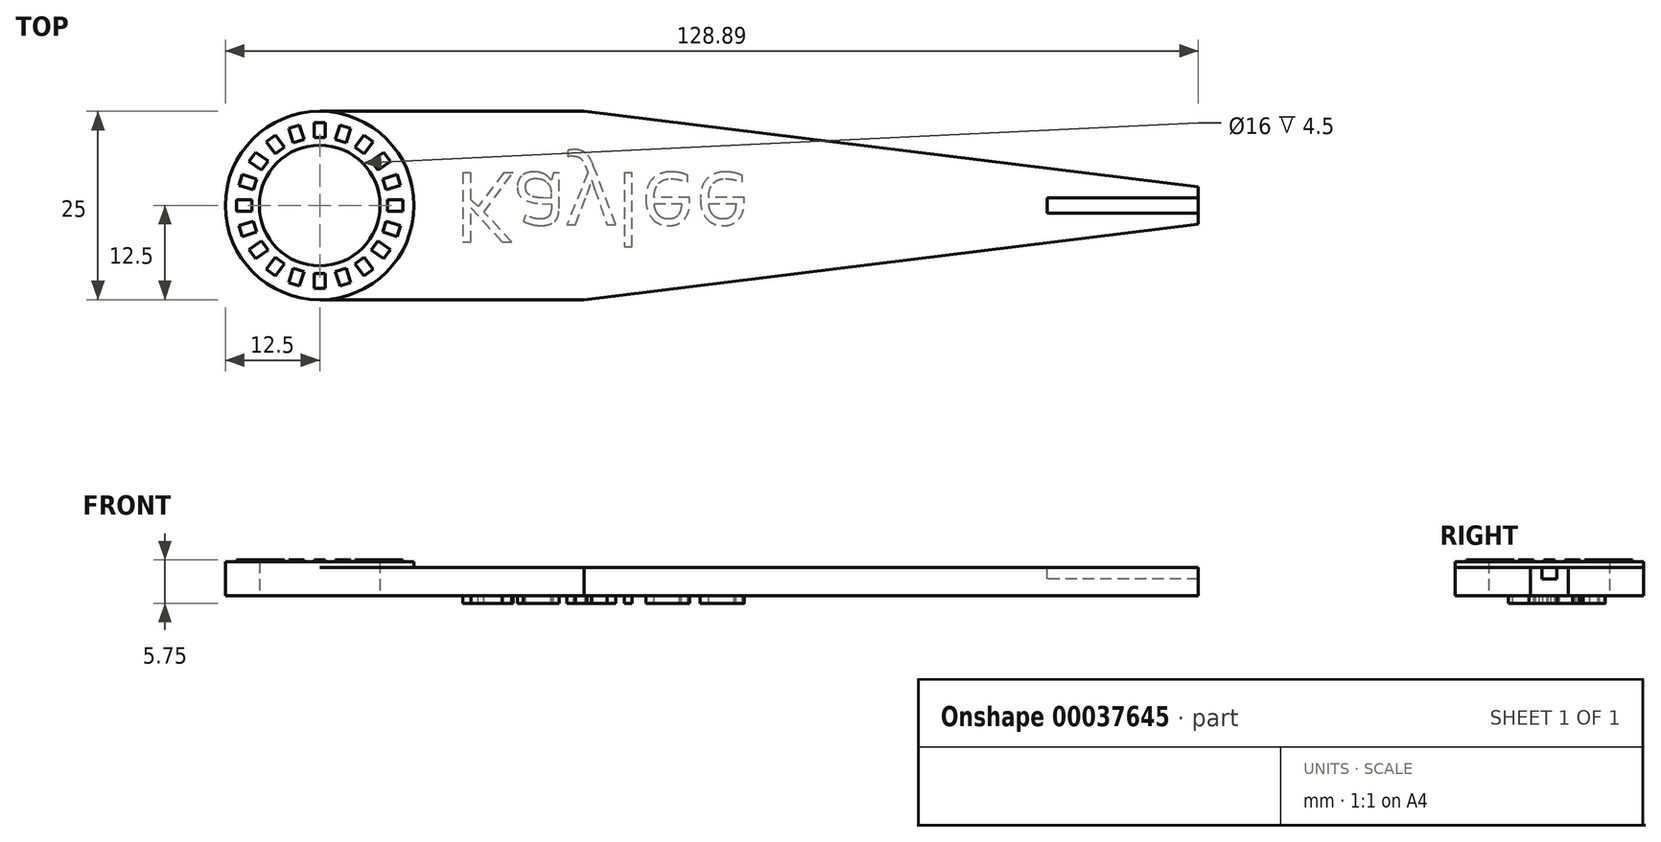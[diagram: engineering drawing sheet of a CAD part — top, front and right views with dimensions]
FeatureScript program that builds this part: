
annotation { "Feature Type Name" : "Feature", "Feature Type Description" : "" }
export const myFeature = defineFeature(function(context is Context, id is Id, definition is map)
    precondition{}
    {
        {
            var Q0;
            Q0=qCreatedBy(makeId("Top.planeOp"),FACE);
            var sketch = newSketch(context, id + "F0", { "sketchPlane" : qUnion([Q0])});
            skCircle(sketch, "E0", {"center": v(0, 0) * mm, "radius": 8 * mm});
            skCircle(sketch, "E1", {"center": v(0, 0) * mm, "radius": 12.5 * mm});
            skLineSegment(sketch, "E2", {"start": v(0, 12.5) * mm, "end": v(35, 12.5) * mm});
            skPoint(sketch, "E3", {"position": v(0, 12.5) * mm});
            skLineSegment(sketch, "E4", {"start": v(0, 0) * mm, "end": v(35.57, 0) * mm, "construction": true});
            skLineSegment(sketch, "E5.MirrorCS", {"start": v(0, -12.5) * mm, "end": v(35, -12.5) * mm});
            skLineSegment(sketch, "E6", {"start": v(35, 12.5) * mm, "end": v(74.56, 12.5) * mm, "construction": true});
            skLineSegment(sketch, "E7", {"start": v(35, 12.5) * mm, "end": v(116.39, 2.5) * mm});
            skLineSegment(sketch, "E8.MirrorCS", {"start": v(35, -12.5) * mm, "end": v(116.39, -2.5) * mm});
            skLineSegment(sketch, "E9", {"start": v(116.39, 2.5) * mm, "end": v(116.39, -2.5) * mm});
            skSolve(sketch);
        }
        {
            var Q0;
            Q0 = qSketchRegion(id + "F0", true);
            extrude(context, id + "F1", {"entities" : qUnion([Q0]), "depth" : 3.5 * mm});
        }
        {
            var Q0;
            Q0=makeQuery(id+"F1.opExtrude","CAP_FACE",FACE,{"disambiguationData":[OSD([sQuery(id+"F0.wireOp",EDGE,"E0"),sQuery(id+"F0.wireOp",EDGE,"E1"),sQuery(id+"F0.wireOp",EDGE,"E2"),sQuery(id+"F0.wireOp",EDGE,"E5.MirrorCS"),sQuery(id+"F0.wireOp",EDGE,"E7"),sQuery(id+"F0.wireOp",EDGE,"E8.MirrorCS"),sQuery(id+"F0.wireOp",EDGE,"E9")])],"isStart":false});
            var sketch = newSketch(context, id + "F2", { "sketchPlane" : qUnion([Q0])});
            skCircle(sketch, "E10", {"center": v(0, 0) * mm, "radius": 12.5 * mm});
            skCircle(sketch, "E11", {"center": v(0, 0) * mm, "radius": 8 * mm});
            skSolve(sketch);
        }
        {
            var Q0;
            Q0 = qSketchRegion(id + "F2", true);
            extrude(context, id + "F3", {"entities" : qUnion([Q0]), "operationType" : NewBodyOperationType.ADD, "depth" : 1 * mm});
        }
        {
            var Q0;
            Q0=makeQuery(id+"F3.opExtrude","CAP_FACE",FACE,{"disambiguationData":[OSD([sQuery(id+"F2.wireOp",EDGE,"E10"),sQuery(id+"F2.wireOp",EDGE,"E11")])],"isStart":false});
            var sketch = newSketch(context, id + "F4", { "sketchPlane" : qUnion([Q0])});
            skLineSegment(sketch, "E12.bottom", {"start": v(-0.75, 11) * mm, "end": v(0.75, 11) * mm});
            skLineSegment(sketch, "E12.top", {"start": v(-0.75, 9) * mm, "end": v(0.75, 9) * mm});
            skLineSegment(sketch, "E12.left", {"start": v(-0.75, 11) * mm, "end": v(-0.75, 9) * mm});
            skLineSegment(sketch, "E12.right", {"start": v(0.75, 11) * mm, "end": v(0.75, 9) * mm});
            skPoint(sketch, "E13", {"position": v(0, 8) * mm});
            skLineSegment(sketch, "E14.1.0", {"start": v(-4.11, 10.23) * mm, "end": v(-2.69, 10.7) * mm});
            skLineSegment(sketch, "E14.1.1", {"start": v(-4.11, 10.23) * mm, "end": v(-3.5, 8.33) * mm});
            skLineSegment(sketch, "E14.1.2", {"start": v(-3.5, 8.33) * mm, "end": v(-2.07, 8.8) * mm});
            skLineSegment(sketch, "E14.1.3", {"start": v(-2.69, 10.7) * mm, "end": v(-2.07, 8.8) * mm});
            skLineSegment(sketch, "E14.2.0", {"start": v(-7.07, 8.46) * mm, "end": v(-5.86, 9.34) * mm});
            skLineSegment(sketch, "E14.2.1", {"start": v(-7.07, 8.46) * mm, "end": v(-5.9, 6.84) * mm});
            skLineSegment(sketch, "E14.2.2", {"start": v(-5.9, 6.84) * mm, "end": v(-4.68, 7.72) * mm});
            skLineSegment(sketch, "E14.2.3", {"start": v(-5.86, 9.34) * mm, "end": v(-4.68, 7.72) * mm});
            skLineSegment(sketch, "E14.3.0", {"start": v(-9.34, 5.86) * mm, "end": v(-8.46, 7.07) * mm});
            skLineSegment(sketch, "E14.3.1", {"start": v(-9.34, 5.86) * mm, "end": v(-7.72, 4.68) * mm});
            skLineSegment(sketch, "E14.3.2", {"start": v(-7.72, 4.68) * mm, "end": v(-6.84, 5.9) * mm});
            skLineSegment(sketch, "E14.3.3", {"start": v(-8.46, 7.07) * mm, "end": v(-6.84, 5.9) * mm});
            skLineSegment(sketch, "E14.4.0", {"start": v(-10.7, 2.69) * mm, "end": v(-10.23, 4.11) * mm});
            skLineSegment(sketch, "E14.4.1", {"start": v(-10.7, 2.69) * mm, "end": v(-8.8, 2.07) * mm});
            skLineSegment(sketch, "E14.4.2", {"start": v(-8.8, 2.07) * mm, "end": v(-8.33, 3.5) * mm});
            skLineSegment(sketch, "E14.4.3", {"start": v(-10.23, 4.11) * mm, "end": v(-8.33, 3.5) * mm});
            skLineSegment(sketch, "E14.5.0", {"start": v(-11, -0.75) * mm, "end": v(-11, 0.75) * mm});
            skLineSegment(sketch, "E14.5.1", {"start": v(-11, -0.75) * mm, "end": v(-9, -0.75) * mm});
            skLineSegment(sketch, "E14.5.2", {"start": v(-9, -0.75) * mm, "end": v(-9, 0.75) * mm});
            skLineSegment(sketch, "E14.5.3", {"start": v(-11, 0.75) * mm, "end": v(-9, 0.75) * mm});
            skLineSegment(sketch, "E14.6.0", {"start": v(-10.23, -4.11) * mm, "end": v(-10.7, -2.69) * mm});
            skLineSegment(sketch, "E14.6.1", {"start": v(-10.23, -4.11) * mm, "end": v(-8.33, -3.5) * mm});
            skLineSegment(sketch, "E14.6.2", {"start": v(-8.33, -3.5) * mm, "end": v(-8.8, -2.07) * mm});
            skLineSegment(sketch, "E14.6.3", {"start": v(-10.7, -2.69) * mm, "end": v(-8.8, -2.07) * mm});
            skLineSegment(sketch, "E14.7.0", {"start": v(-8.46, -7.07) * mm, "end": v(-9.34, -5.86) * mm});
            skLineSegment(sketch, "E14.7.1", {"start": v(-8.46, -7.07) * mm, "end": v(-6.84, -5.9) * mm});
            skLineSegment(sketch, "E14.7.2", {"start": v(-6.84, -5.9) * mm, "end": v(-7.72, -4.68) * mm});
            skLineSegment(sketch, "E14.7.3", {"start": v(-9.34, -5.86) * mm, "end": v(-7.72, -4.68) * mm});
            skLineSegment(sketch, "E14.8.0", {"start": v(-5.86, -9.34) * mm, "end": v(-7.07, -8.46) * mm});
            skLineSegment(sketch, "E14.8.1", {"start": v(-5.86, -9.34) * mm, "end": v(-4.68, -7.72) * mm});
            skLineSegment(sketch, "E14.8.2", {"start": v(-4.68, -7.72) * mm, "end": v(-5.9, -6.84) * mm});
            skLineSegment(sketch, "E14.8.3", {"start": v(-7.07, -8.46) * mm, "end": v(-5.9, -6.84) * mm});
            skLineSegment(sketch, "E14.9.0", {"start": v(-2.69, -10.7) * mm, "end": v(-4.11, -10.23) * mm});
            skLineSegment(sketch, "E14.9.1", {"start": v(-2.69, -10.7) * mm, "end": v(-2.07, -8.8) * mm});
            skLineSegment(sketch, "E14.9.2", {"start": v(-2.07, -8.8) * mm, "end": v(-3.5, -8.33) * mm});
            skLineSegment(sketch, "E14.9.3", {"start": v(-4.11, -10.23) * mm, "end": v(-3.5, -8.33) * mm});
            skLineSegment(sketch, "E14.10.0", {"start": v(0.75, -11) * mm, "end": v(-0.75, -11) * mm});
            skLineSegment(sketch, "E14.10.1", {"start": v(0.75, -11) * mm, "end": v(0.75, -9) * mm});
            skLineSegment(sketch, "E14.10.2", {"start": v(0.75, -9) * mm, "end": v(-0.75, -9) * mm});
            skLineSegment(sketch, "E14.10.3", {"start": v(-0.75, -11) * mm, "end": v(-0.75, -9) * mm});
            skLineSegment(sketch, "E14.11.0", {"start": v(4.11, -10.23) * mm, "end": v(2.69, -10.7) * mm});
            skLineSegment(sketch, "E14.11.1", {"start": v(4.11, -10.23) * mm, "end": v(3.5, -8.33) * mm});
            skLineSegment(sketch, "E14.11.2", {"start": v(3.5, -8.33) * mm, "end": v(2.07, -8.8) * mm});
            skLineSegment(sketch, "E14.11.3", {"start": v(2.69, -10.7) * mm, "end": v(2.07, -8.8) * mm});
            skLineSegment(sketch, "E14.12.0", {"start": v(7.07, -8.46) * mm, "end": v(5.86, -9.34) * mm});
            skLineSegment(sketch, "E14.12.1", {"start": v(7.07, -8.46) * mm, "end": v(5.9, -6.84) * mm});
            skLineSegment(sketch, "E14.12.2", {"start": v(5.9, -6.84) * mm, "end": v(4.68, -7.72) * mm});
            skLineSegment(sketch, "E14.12.3", {"start": v(5.86, -9.34) * mm, "end": v(4.68, -7.72) * mm});
            skLineSegment(sketch, "E14.13.0", {"start": v(9.34, -5.86) * mm, "end": v(8.46, -7.07) * mm});
            skLineSegment(sketch, "E14.13.1", {"start": v(9.34, -5.86) * mm, "end": v(7.72, -4.68) * mm});
            skLineSegment(sketch, "E14.13.2", {"start": v(7.72, -4.68) * mm, "end": v(6.84, -5.9) * mm});
            skLineSegment(sketch, "E14.13.3", {"start": v(8.46, -7.07) * mm, "end": v(6.84, -5.9) * mm});
            skLineSegment(sketch, "E14.14.0", {"start": v(10.7, -2.69) * mm, "end": v(10.23, -4.11) * mm});
            skLineSegment(sketch, "E14.14.1", {"start": v(10.7, -2.69) * mm, "end": v(8.8, -2.07) * mm});
            skLineSegment(sketch, "E14.14.2", {"start": v(8.8, -2.07) * mm, "end": v(8.33, -3.5) * mm});
            skLineSegment(sketch, "E14.14.3", {"start": v(10.23, -4.11) * mm, "end": v(8.33, -3.5) * mm});
            skLineSegment(sketch, "E14.15.0", {"start": v(11, 0.75) * mm, "end": v(11, -0.75) * mm});
            skLineSegment(sketch, "E14.15.1", {"start": v(11, 0.75) * mm, "end": v(9, 0.75) * mm});
            skLineSegment(sketch, "E14.15.2", {"start": v(9, 0.75) * mm, "end": v(9, -0.75) * mm});
            skLineSegment(sketch, "E14.15.3", {"start": v(11, -0.75) * mm, "end": v(9, -0.75) * mm});
            skLineSegment(sketch, "E14.16.0", {"start": v(10.23, 4.11) * mm, "end": v(10.7, 2.69) * mm});
            skLineSegment(sketch, "E14.16.1", {"start": v(10.23, 4.11) * mm, "end": v(8.33, 3.5) * mm});
            skLineSegment(sketch, "E14.16.2", {"start": v(8.33, 3.5) * mm, "end": v(8.8, 2.07) * mm});
            skLineSegment(sketch, "E14.16.3", {"start": v(10.7, 2.69) * mm, "end": v(8.8, 2.07) * mm});
            skLineSegment(sketch, "E14.17.0", {"start": v(8.46, 7.07) * mm, "end": v(9.34, 5.86) * mm});
            skLineSegment(sketch, "E14.17.1", {"start": v(8.46, 7.07) * mm, "end": v(6.84, 5.9) * mm});
            skLineSegment(sketch, "E14.17.2", {"start": v(6.84, 5.9) * mm, "end": v(7.72, 4.68) * mm});
            skLineSegment(sketch, "E14.17.3", {"start": v(9.34, 5.86) * mm, "end": v(7.72, 4.68) * mm});
            skLineSegment(sketch, "E14.18.0", {"start": v(5.86, 9.34) * mm, "end": v(7.07, 8.46) * mm});
            skLineSegment(sketch, "E14.18.1", {"start": v(5.86, 9.34) * mm, "end": v(4.68, 7.72) * mm});
            skLineSegment(sketch, "E14.18.2", {"start": v(4.68, 7.72) * mm, "end": v(5.9, 6.84) * mm});
            skLineSegment(sketch, "E14.18.3", {"start": v(7.07, 8.46) * mm, "end": v(5.9, 6.84) * mm});
            skLineSegment(sketch, "E14.19.0", {"start": v(2.69, 10.7) * mm, "end": v(4.11, 10.23) * mm});
            skLineSegment(sketch, "E14.19.1", {"start": v(2.69, 10.7) * mm, "end": v(2.07, 8.8) * mm});
            skLineSegment(sketch, "E14.19.2", {"start": v(2.07, 8.8) * mm, "end": v(3.5, 8.33) * mm});
            skLineSegment(sketch, "E14.19.3", {"start": v(4.11, 10.23) * mm, "end": v(3.5, 8.33) * mm});
            skPoint(sketch, "E14.center", {"position": v(0, 0) * mm});
            skSolve(sketch);
        }
        {
            var Q0;
            Q0 = qSketchRegion(id + "F4", true);
            extrude(context, id + "F5", {"entities" : qUnion([Q0]), "operationType" : NewBodyOperationType.ADD, "depth" : .25 * mm});
        }
        {
            var Q0;
            Q0=makeQuery(id+"F1.opExtrude","CAP_FACE",FACE,{"disambiguationData":[OSD([sQuery(id+"F0.wireOp",EDGE,"E0"),sQuery(id+"F0.wireOp",EDGE,"E1"),sQuery(id+"F0.wireOp",EDGE,"E2"),sQuery(id+"F0.wireOp",EDGE,"E5.MirrorCS"),sQuery(id+"F0.wireOp",EDGE,"E7"),sQuery(id+"F0.wireOp",EDGE,"E8.MirrorCS"),sQuery(id+"F0.wireOp",EDGE,"E9")])],"isStart":false});
            var sketch = newSketch(context, id + "F6", { "sketchPlane" : qUnion([Q0])});
            skSolve(sketch);
        }
        {
            var Q0;
            Q0=makeQuery(id+"F6.imprint","IMPRINT",FACE,{"disambiguationData":[TD([[makeQuery(id+"F6.imprint","IMPRINT",EDGE,{"derivedFrom":makeQuery(id+"F1.opExtrude","CAP_EDGE",EDGE,{"disambiguationData":[OSD([sQuery(id+"F0.wireOp",EDGE,"E2")])],"isStart":false})}),-1.0]])]});
            var Q1;
            Q1 = qSketchRegion(id + "FdAY0HOer0T3xGX_1", true);
            extrude(context, id + "F7", {"entities" : qUnion([Q0, Q1]), "operationType" : NewBodyOperationType.ADD, "depth" : .25 * mm});
        }
        {
            var Q0;
            Q0=makeQuery(id+"F1.opExtrude","CAP_FACE",FACE,{"disambiguationData":[OSD([sQuery(id+"F0.wireOp",EDGE,"E0"),sQuery(id+"F0.wireOp",EDGE,"E1"),sQuery(id+"F0.wireOp",EDGE,"E2"),sQuery(id+"F0.wireOp",EDGE,"E5.MirrorCS"),sQuery(id+"F0.wireOp",EDGE,"E7"),sQuery(id+"F0.wireOp",EDGE,"E8.MirrorCS"),sQuery(id+"F0.wireOp",EDGE,"E9")])],"isStart":true});
            var sketch = newSketch(context, id + "F8", { "sketchPlane" : qUnion([Q0])});
            skText(sketch, "E15", { "text": "Kaylee", "fontName": "OpenSans-Regular.ttf"});
            const initialGuessF8  = {"E15": [0.0177, -0.00433, 1, 0, 0.00926]};
            skSetInitialGuess(sketch, initialGuessF8);
            skSolve(sketch);
        }
        {
            var Q0;
            Q0 = qSketchRegion(id + "F8", true);
            extrude(context, id + "F9", {"entities" : qUnion([Q0]), "operationType" : NewBodyOperationType.ADD, "depth" : 1 * mm});
        }
        {
            var Q0;
            Q0=makeQuery(id+"F7.opExtrude","CAP_FACE",FACE,{"disambiguationData":[OSD([sQuery(id+"F0.wireOp",EDGE,"E2"),sQuery(id+"F0.wireOp",EDGE,"E5.MirrorCS"),sQuery(id+"F0.wireOp",EDGE,"E7"),sQuery(id+"F0.wireOp",EDGE,"E8.MirrorCS"),sQuery(id+"F0.wireOp",EDGE,"E9"),sQuery(id+"F2.wireOp",EDGE,"E10")])],"isStart":false});
            var sketch = newSketch(context, id + "F10", { "sketchPlane" : qUnion([Q0])});
            skLineSegment(sketch, "E16.bottom", {"start": v(116.39, 1) * mm, "end": v(96.39, 1) * mm});
            skLineSegment(sketch, "E16.top", {"start": v(116.39, -1) * mm, "end": v(96.39, -1) * mm});
            skLineSegment(sketch, "E16.left", {"start": v(116.39, 1) * mm, "end": v(116.39, -1) * mm});
            skLineSegment(sketch, "E16.right", {"start": v(96.39, 1) * mm, "end": v(96.39, -1) * mm});
            skSolve(sketch);
        }
        {
            var Q0;
            Q0 = qSketchRegion(id + "F10", true);
            extrude(context, id + "F11", {"entities" : qUnion([Q0]), "operationType" : NewBodyOperationType.REMOVE, "oppositeDirection" : true, "depth" : 1.5 * mm});
        }
    });
